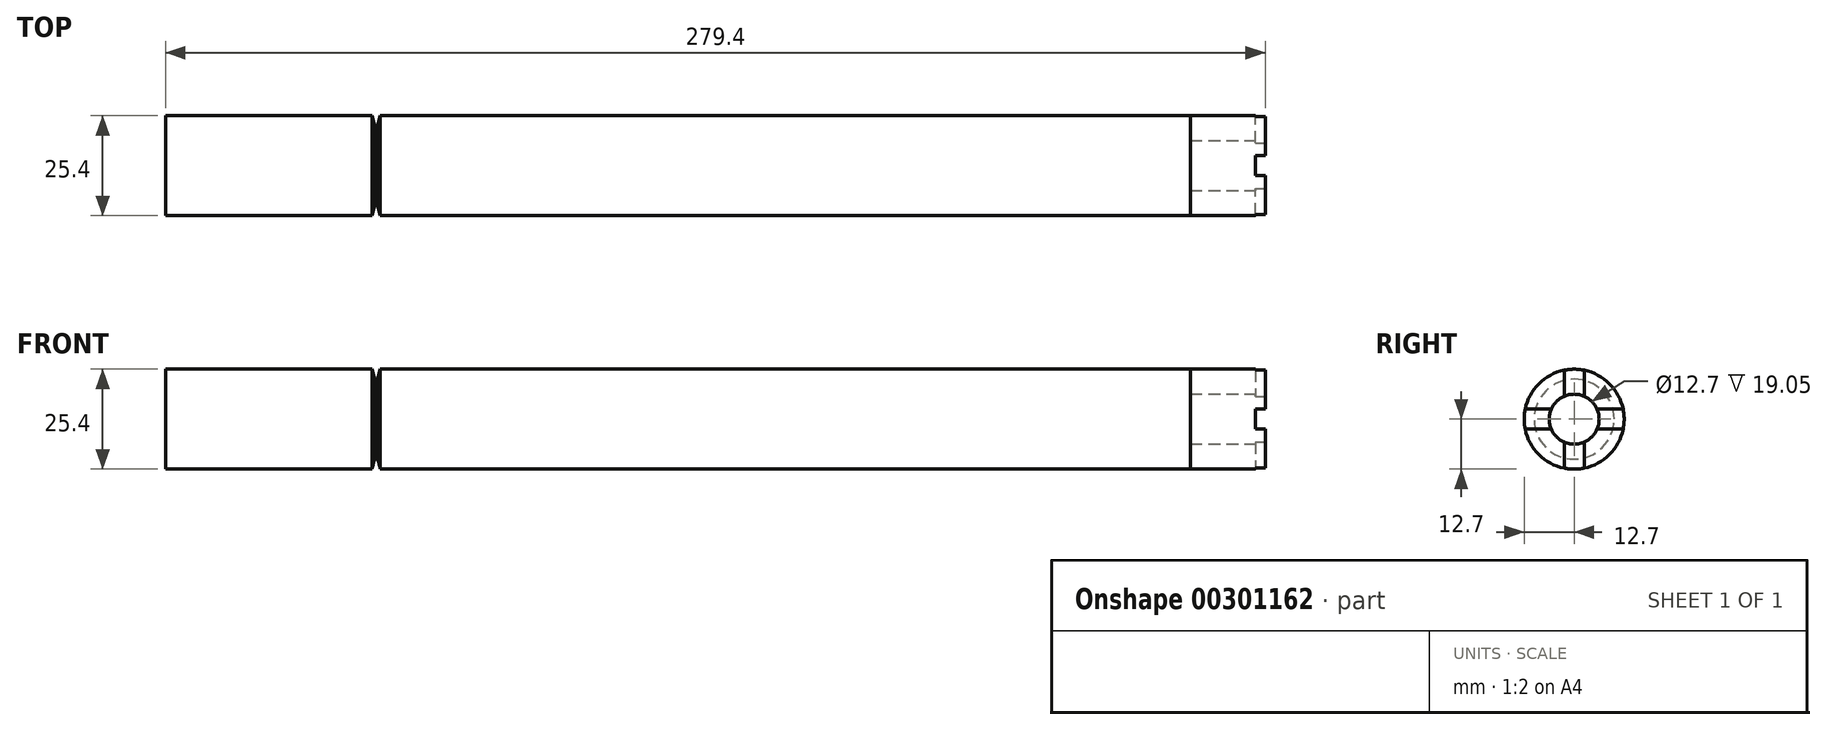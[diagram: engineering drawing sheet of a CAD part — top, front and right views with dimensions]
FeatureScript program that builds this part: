
annotation { "Feature Type Name" : "Feature", "Feature Type Description" : "" }
export const myFeature = defineFeature(function(context is Context, id is Id, definition is map)
    precondition{}
    {
        {
            var Q0;
            Q0=qCreatedBy(makeId("Front.planeOp"),FACE);
            var sketch = newSketch(context, id + "F0", { "sketchPlane" : qUnion([Q0])});
            skLineSegment(sketch, "E0", {"start": v(-139.7, 0) * mm, "end": v(139.7, 0) * mm});
            skLineSegment(sketch, "E1", {"start": v(139.7, 0) * mm, "end": v(139.7, 12.7) * mm});
            skLineSegment(sketch, "E2", {"start": v(139.7, 12.7) * mm, "end": v(-139.7, 12.7) * mm});
            skLineSegment(sketch, "E3", {"start": v(-139.7, 12.7) * mm, "end": v(-139.7, 0) * mm});
            skLineSegment(sketch, "E4", {"start": v(-177.14, 0) * mm, "end": v(149.47, 0) * mm, "construction": true});
            skSolve(sketch);
        }
        {
            var Q0;
            Q0 = qSketchRegion(id + "F0", true);
            var Q1;
            Q1=sQuery(id+"F0.wireOp",EDGE,"E4");
            revolve(context, id + "F1", {"entities" : qUnion([Q0]), "axis" : qUnion([Q1]), "revolveType" : RevolveType.FULL});
        }
        {
            var Q0;
            Q0=makeQuery(id+"F1.opRevolve","SWEPT_FACE",FACE,{"disambiguationData":[OSD([sQuery(id+"F0.wireOp",EDGE,"E1")])]});
            cPlane(context, id + "F2", {"entities" : qUnion([Q0]), "cplaneType" : CPlaneType.OFFSET, "offset" : 25.4 * mm, "width" : 152.4 * mm, "height" : 152.4 * mm});
        }
        {
            var Q0;
            Q0=qCreatedBy(id+"F2.planeOp",FACE);
            var sketch = newSketch(context, id + "F3", { "sketchPlane" : qUnion([Q0])});
            skCircle(sketch, "E5", {"center": v(0, 0) * mm, "radius": 6.35 * mm});
            skSolve(sketch);
        }
        {
            var Q0;
            Q0 = qSketchRegion(id + "F3", true);
            extrude(context, id + "F4", {"entities" : qUnion([Q0]), "operationType" : NewBodyOperationType.REMOVE, "oppositeDirection" : true, "depth" : 44.45 * mm});
        }
        {
            var Q0;
            Q0=makeQuery(id+"F1.opRevolve","SWEPT_FACE",FACE,{"disambiguationData":[OSD([sQuery(id+"F0.wireOp",EDGE,"E1")])]});
            var sketch = newSketch(context, id + "F5", { "sketchPlane" : qUnion([Q0])});
            skLineSegment(sketch, "E6", {"start": v(-12.44, 2.54) * mm, "end": v(12.44, 2.54) * mm});
            skLineSegment(sketch, "E7", {"start": v(-12.44, -2.54) * mm, "end": v(12.44, -2.54) * mm});
            skArc(sketch, "E8", {"start": v(-12.44, 2.54) * mm, "mid": v(-14.98, 0) * mm, "end": v(-12.44, -2.54) * mm});
            skArc(sketch, "E9", {"start": v(12.44, 2.54) * mm, "mid": v(14.98, 0) * mm, "end": v(12.44, -2.54) * mm});
            skSolve(sketch);
        }
        {
            var Q0;
            Q0 = qSketchRegion(id + "F5", true);
            extrude(context, id + "F6", {"entities" : qUnion([Q0]), "operationType" : NewBodyOperationType.REMOVE, "oppositeDirection" : true, "depth" : 2.54 * mm});
        }
        {
            var Q0;
            Q0=makeQuery(id+"F6.boolean.opBoolean","SPLIT",FACE,{"disambiguationData":[TD([makeQuery(id+"F6.opExtrude","SWEPT_FACE",FACE,{"disambiguationData":[OSD([sQuery(id+"F5.wireOp",EDGE,"E6")])]})])],"derivedFrom":makeQuery(id+"F1.opRevolve","SWEPT_FACE",FACE,{"disambiguationData":[OSD([sQuery(id+"F0.wireOp",EDGE,"E1")])]})});
            var sketch = newSketch(context, id + "F7", { "sketchPlane" : qUnion([Q0])});
            skLineSegment(sketch, "E10", {"start": v(2.54, 12.44) * mm, "end": v(2.54, -12.44) * mm});
            skLineSegment(sketch, "E11", {"start": v(-2.54, 12.44) * mm, "end": v(-2.54, -12.44) * mm});
            skArc(sketch, "E12", {"start": v(-2.54, -12.44) * mm, "mid": v(0, -14.98) * mm, "end": v(2.54, -12.44) * mm});
            skArc(sketch, "E13", {"start": v(-2.54, 12.44) * mm, "mid": v(0, 14.98) * mm, "end": v(2.54, 12.44) * mm});
            skSolve(sketch);
        }
        {
            var Q0;
            Q0 = qSketchRegion(id + "F7", true);
            extrude(context, id + "F8", {"entities" : qUnion([Q0]), "operationType" : NewBodyOperationType.REMOVE, "oppositeDirection" : true, "depth" : 2.54 * mm});
        }
        {
            var Q0;
            Q0=qCreatedBy(makeId("Right.planeOp"),FACE);
            var sketch = newSketch(context, id + "F9", { "sketchPlane" : qUnion([Q0])});
            skCircle(sketch, "E14", {"center": v(0, 0) * mm, "radius": 12.7 * mm});
            skSolve(sketch);
        }
        {
            var Q0;
            Q0 = qSketchRegion(id + "F9", true);
            extrude(context, id + "F10", {"entities" : qUnion([Q0]), "oppositeDirection" : true, "depth" : 87.25 * mm, "hasSecondDirection" : true, "secondDirectionOppositeDirection" : false, "secondDirectionDepth" : 120.65 * mm});
        }
        {
            var Q0;
            Q0=qCreatedBy(makeId("Front.planeOp"),FACE);
            var sketch = newSketch(context, id + "F11", { "sketchPlane" : qUnion([Q0])});
            skLineSegment(sketch, "E15", {"start": v(-86.61, 10.16) * mm, "end": v(-85.78, 10.16) * mm});
            skLineSegment(sketch, "E16", {"start": v(-85.78, 10.16) * mm, "end": v(-85.14, 12.7) * mm});
            skLineSegment(sketch, "E17", {"start": v(-85.14, 12.7) * mm, "end": v(-87.25, 12.7) * mm});
            skLineSegment(sketch, "E18", {"start": v(-87.25, 12.7) * mm, "end": v(-86.61, 10.16) * mm});
            skSolve(sketch);
        }
        {
            var Q0;
            Q0 = qSketchRegion(id + "F11", true);
            var Q1;
            Q1=sQuery(id+"F0.wireOp",EDGE,"E4");
            revolve(context, id + "F12", {"operationType" : NewBodyOperationType.REMOVE, "entities" : qUnion([Q0]), "axis" : qUnion([Q1]), "revolveType" : RevolveType.FULL, "oppositeDirection" : true});
        }
    });
